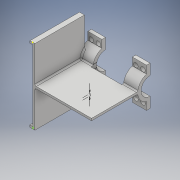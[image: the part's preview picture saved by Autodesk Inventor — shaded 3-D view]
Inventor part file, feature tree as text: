
AUTODESK INVENTOR PART (.ipt)
format: ipt  version: 2018 (Build 220112000, 112)  size: 487,424 bytes
history: native  units: mm
features: sketch x11, extrude x10, fillet x1
ambient origin geometry x8: Origin, YZ Plane, XZ Plane, XY Plane, X Axis, Y Axis, Z Axis, Center Point
bodies: Solid1 (feature_tree)
feature tree (22):
  extrude  "Extrusion1"  Depth=106.0mm
  sketch  "Sketch2"  dims[d2=80.0mm d3=3.0mm]
  sketch  "Sketch3"  dims[d4=70.0mm d5=0.0mm d6=3.0mm]
  sketch  "Sketch4"  dims[d7=3.0mm d8=3.0mm]
  extrude  "Extrusion2"  Depth=3.0mm
  extrude  "Extrusion3"  Depth=3.0mm
  extrude  "Extrusion4"  Depth=3.0mm
  extrude  "Extrusion5"  Depth=4.0mm TaperAngle=0.0deg
  extrude  "Extrusion6"  Depth=12.7mm
  extrude  "Extrusion7"  Depth=20.0mm TaperAngle=0.0deg
  fillet  "Fillet1"  Radius=20.0mm
  extrude  "Extrusion8"  Depth=15.0mm
  extrude  "Extrusion9"  Depth=15.0mm
  extrude  "Extrusion10"  Depth=5.0mm TaperAngle=0.0deg
  sketch  "Sketch1"  dims[d0=3.0mm d1=106.0mm]
  sketch  "Sketch5"  dims[d9=4.0mm d10=0.0mm d11=4.0mm d12=0.0mm]
  sketch  "Sketch6"  dims[d13=12.7mm d14=25.4mm]
  sketch  "Sketch7"  dims[d15=35.0mm d16=20.0mm d17=0.0mm d18=20.0mm d19=0.0mm]
  sketch  "Sketch8"  dims[d20=2000.0mm d21=0.0mm d22=15.0mm]
  sketch  "Sketch9"  dims[d23=15.0mm d24=15.0mm]
  sketch  "Sketch10"  dims[d25=20.0mm d26=5.0mm d27=0.0mm]
  sketch  "Sketch11"  dims[d28=2.0mm d29=7.5mm d30=0.0mm d31=6.35mm d32=6.35mm d33=6.35mm d34=6.35mm d35=7.5mm d36=0.0mm d37=6.35mm d38=6.35mm d39=6.35mm d40=6.35mm d41=7.5mm d42=0.0mm]
